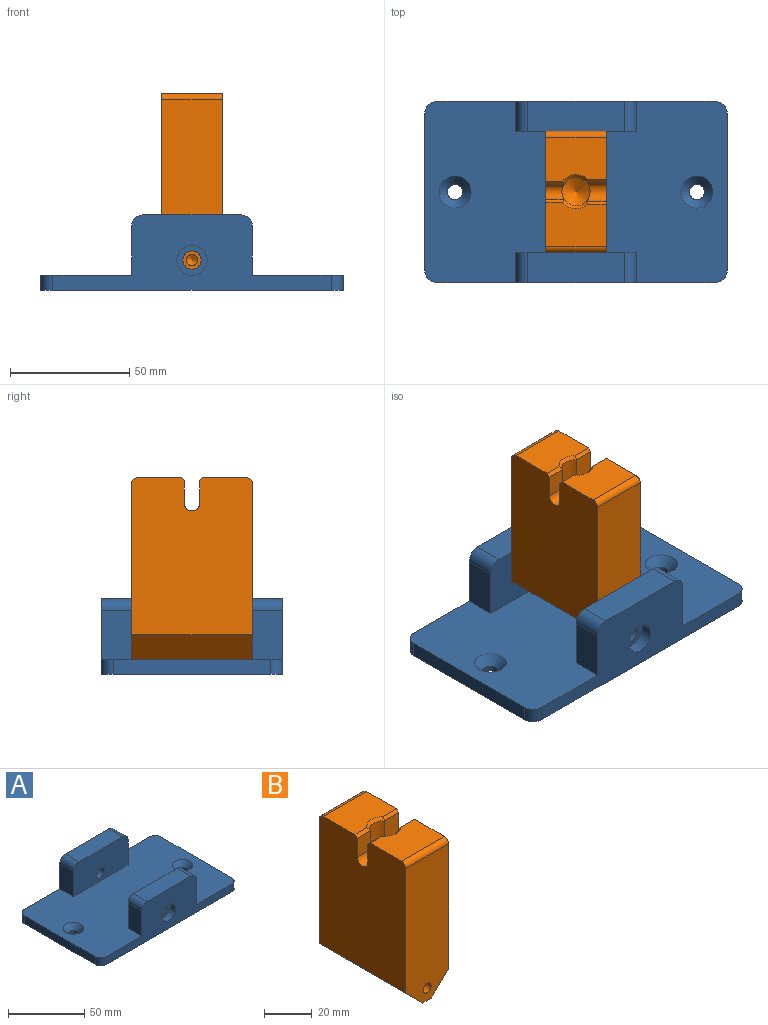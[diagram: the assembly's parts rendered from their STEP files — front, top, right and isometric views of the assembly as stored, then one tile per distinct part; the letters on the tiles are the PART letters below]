
ASSEMBLY  parts=2 mates=1
PART A: 32 faces, bbox 127x76.2x31.8 mm
  f0: plane 127x76.2mm, normal (0,0,1), area 8080.3mm2, adj f1,f2,f3,f4,f5,f6,f7,f8
  f1: plane 66.04x6.35mm, normal (1,0,0), area 419.4mm2, adj f0,f2,f8,f9
  f2: cylinder r=5.08mm len=6.35mm, axis (0,0,1), area 50.7mm2, adj f0,f1,f3,f9
  f3: plane 116.84x31.75mm, normal (0,1,0), area 1894.5mm2, adj f0,f2,f4,f9,f14,f15,f17,f18
  f4: cylinder r=5.08mm len=6.35mm, axis (0,0,1), area 50.7mm2, adj f0,f3,f5,f9
  f5: plane 66.04x6.35mm, normal (-1,0,0), area 419.4mm2, adj f0,f4,f6,f9
  f6: cylinder r=5.08mm len=6.35mm, axis (0,0,1), area 50.7mm2, adj f0,f5,f7,f9
  f7: plane 116.84x31.75mm, normal (0,-1,0), area 1894.5mm2, adj f0,f6,f8,f9,f10,f12,f13,f20
  f8: cylinder r=5.08mm len=6.35mm, axis (0,0,1), area 50.7mm2, adj f0,f1,f7,f9
  f9: plane 127x76.2mm, normal (0,0,-1), area 9591.9mm2, adj f1,f2,f3,f4,f5,f6,f7,f8
  f10: plane 20.32x12.7mm, normal (-1,0,0), area 258.1mm2, adj f0,f7,f11,f20
  f11: plane 50.8x25.4mm, normal (0,1,0), area 1233.6mm2, adj f0,f10,f12,f13,f20,f21,f29
  f12: plane 20.32x12.7mm, normal (1,0,0), area 258.1mm2, adj f0,f7,f11,f21
  f13: plane 40.64x12.7mm, normal (0,0,1), area 516.1mm2, adj f7,f11,f20,f21
  f14: plane 20.32x12.7mm, normal (-1,0,0), area 258.1mm2, adj f0,f3,f16,f19
  f15: plane 20.32x12.7mm, normal (1,0,0), area 258.1mm2, adj f0,f3,f16,f18
  f16: plane 50.8x25.4mm, normal (0,-1,0), area 1233.6mm2, adj f0,f14,f15,f17,f18,f19,f26
  f17: plane 40.64x12.7mm, normal (0,0,1), area 516.1mm2, adj f3,f16,f18,f19
  f18: cylinder r=5.08mm len=12.7mm, axis (0,1,0), area 101.3mm2, adj f3,f15,f16,f17
  f19: cylinder r=5.08mm len=12.7mm, axis (0,-1,0), area 101.3mm2, adj f3,f14,f16,f17
  f20: cylinder r=5.08mm len=12.7mm, axis (0,-1,0), area 101.3mm2, adj f7,f10,f11,f13
  f21: cylinder r=5.08mm len=12.7mm, axis (0,1,0), area 101.3mm2, adj f7,f11,f12,f13
  f22: cylinder r=3.17mm len=6.35mm, axis (0,0,1), area 49.3mm2, adj f9,f23
  f23: cone r=3.17mm half-angle=42.5deg, axis (0,0,1), area 163.8mm2, adj f0,f22
  f24: cylinder r=3.17mm len=6.35mm, axis (0,0,1), area 49.3mm2, adj f9,f25
  f25: cone r=3.17mm half-angle=42.5deg, axis (0,0,1), area 163.8mm2, adj f0,f24
  f26: cylinder r=3.81mm len=7.62mm, axis (0,1,0), area 182.4mm2, adj f16,f27
  f27: plane 12.7x12.7mm, normal (0,1,0), area 81.1mm2, adj f26,f28
  f28: cylinder r=6.35mm len=12.7mm, axis (0,1,0), area 202.7mm2, adj f3,f27
  f29: cylinder r=3.81mm len=7.62mm, axis (0,-1,0), area 182.4mm2, adj f11,f30
  f30: plane 12.7x12.7mm, normal (0,-1,0), area 81.1mm2, adj f29,f31
  f31: cylinder r=6.35mm len=12.7mm, axis (0,-1,0), area 202.7mm2, adj f7,f30
PART B: 29 faces, bbox 25.5x50.9x76.3 mm
  f0: plane 25.4x18.42mm, normal (0,0,1), area 439.5mm2, adj f1,f3,f10,f18,f19,f20
  f1: plane 66.04x50.8mm, normal (1,0,0), area 3151.1mm2, adj f0,f2,f6,f7,f8,f10,f11,f15
  f2: plane 25.4x18.42mm, normal (0,0,1), area 439.5mm2, adj f1,f3,f11,f21,f22,f23
  f3: plane 66.04x50.8mm, normal (-1,0,0), area 3266.1mm2, adj f0,f2,f4,f7,f8,f10,f11,f12
  f4: plane 50.8x10.16mm, normal (-0.71,0,-0.71), area 729.9mm2, adj f3,f5,f7,f8
  f5: plane 50.8x5.08mm, normal (0,0,-1), area 258.1mm2, adj f4,f6,f7,f8
  f6: plane 50.8x10.16mm, normal (0.71,0,-0.71), area 729.9mm2, adj f1,f5,f7,f8
  f7: plane 73.66x25.4mm, normal (0,1,0), area 1750.2mm2, adj f1,f3,f4,f5,f6,f11,f27
  f8: plane 73.66x25.4mm, normal (0,-1,0), area 1750.2mm2, adj f1,f3,f4,f5,f6,f10,f25
  f9: cylinder r=5.92mm len=57.15mm, axis (0,0,1), area 1837.2mm2, adj f12,f13,f14,f15,f16,f17,f19,f22
  f10: cylinder r=2.54mm len=25.4mm, axis (-1,0,0), area 101.3mm2, adj f0,f1,f3,f8
  f11: cylinder r=2.54mm len=25.4mm, axis (1,0,0), area 101.3mm2, adj f1,f2,f3,f7
  f12: plane 9.53x7.71mm, normal (0,-1,0), area 73.4mm2, adj f3,f9,f13,f21
  f13: cylinder r=3.17mm len=7.71mm, axis (-1,0,0), area 72.2mm2, adj f3,f9,f12,f14
  f14: plane 9.53x7.71mm, normal (0,1,0), area 73.4mm2, adj f3,f9,f13,f20
  f15: plane 20.07x8.4mm, normal (0,1,0), area 168.5mm2, adj f1,f9,f16,f18
  f16: cylinder r=4.06mm len=8.4mm, axis (1,0,0), area 96.5mm2, adj f1,f9,f15,f17
  f17: plane 20.07x8.4mm, normal (0,-1,0), area 168.5mm2, adj f1,f9,f16,f23
  f18: plane 8.44x1.31mm, normal (0,0.71,0.71), area 14.6mm2, adj f0,f1,f15,f19
  f19: cone r=5.92mm half-angle=45deg, axis (0,0,1), area 20.3mm2, adj f0,f9,f18,f20
  f20: plane 7.76x1.32mm, normal (0,0.71,0.71), area 13.2mm2, adj f0,f3,f14,f19
  f21: plane 7.76x1.32mm, normal (0,-0.71,0.71), area 13.2mm2, adj f2,f3,f12,f22
  f22: cone r=5.92mm half-angle=45deg, axis (0,0,1), area 20.3mm2, adj f2,f9,f21,f23
  f23: plane 8.44x1.31mm, normal (0,-0.71,0.71), area 14.6mm2, adj f1,f2,f17,f22
  f24: cone r=0mm half-angle=59deg, axis (0,-1,0), area 20.5mm2, adj f25
  f25: cylinder r=2.36mm len=15.24mm, axis (0,-1,0), area 226.2mm2, adj f8,f24
  f26: cone r=0mm half-angle=59deg, axis (0,1,0), area 20.5mm2, adj f27
  f27: cylinder r=2.36mm len=15.24mm, axis (0,1,0), area 226.2mm2, adj f7,f26
  f28: cone r=0mm half-angle=59deg, axis (0,0,1), area 128.4mm2, adj f9
PLACE A t=(-5.31,-63.51,22.87)mm
PLACE B t=(-30.71,-50.81,22.87)mm
MATE revolute A.f26 <-> B.f24  axis (0,-1,0) through (-68.81,-0.01,29.22)mm
